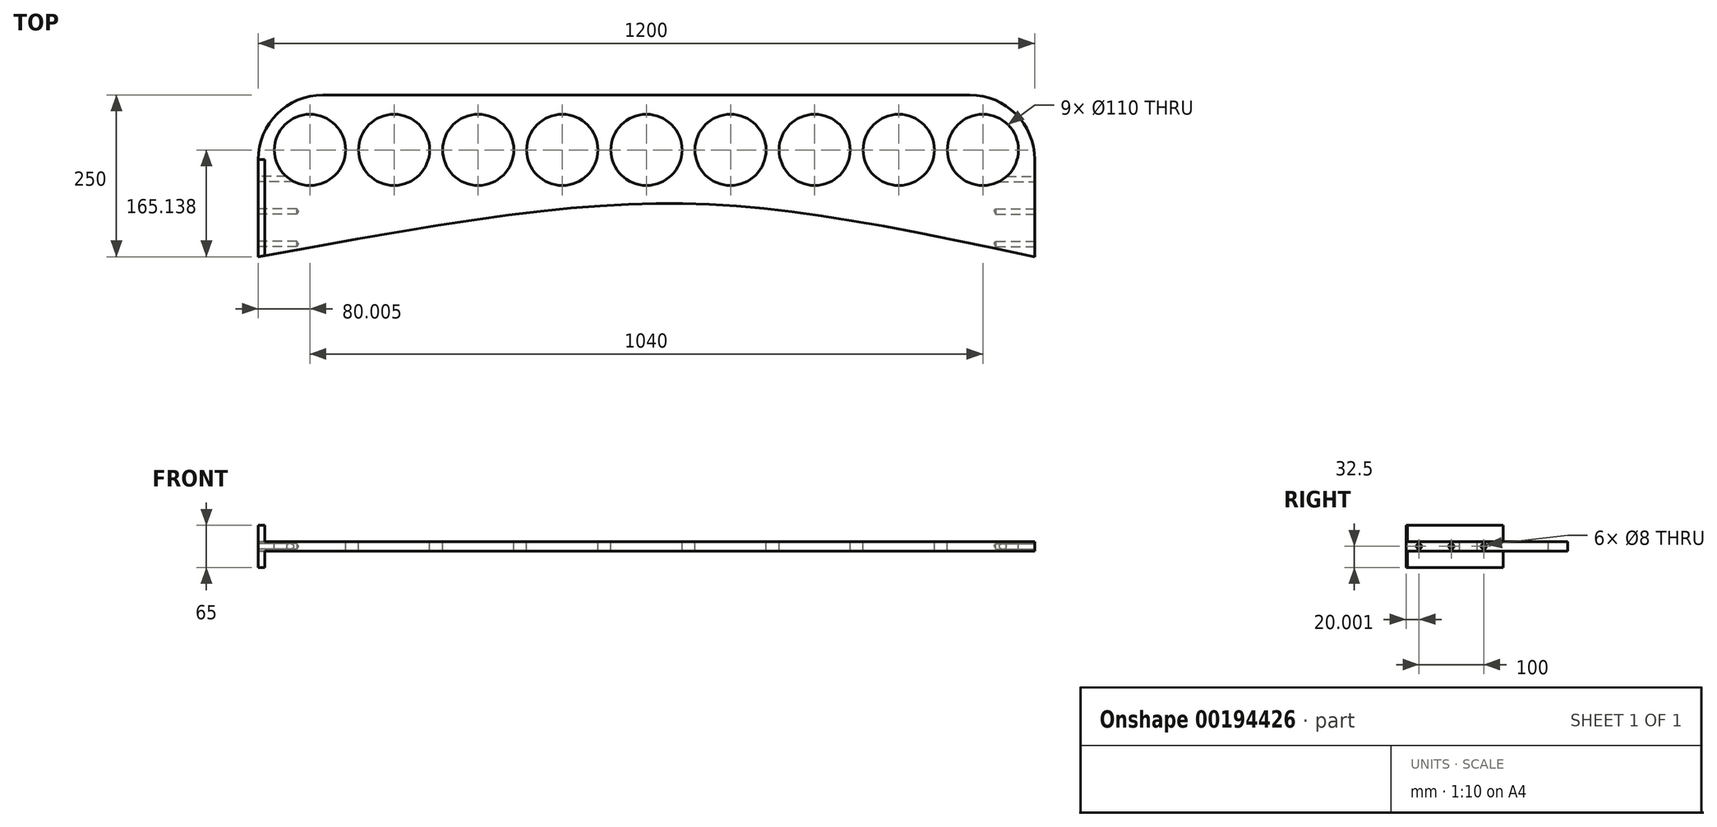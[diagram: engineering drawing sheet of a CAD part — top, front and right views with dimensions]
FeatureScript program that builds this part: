
annotation { "Feature Type Name" : "Feature", "Feature Type Description" : "" }
export const myFeature = defineFeature(function(context is Context, id is Id, definition is map)
    precondition{}
    {
        {
            var Q0;
            Q0=qCreatedBy(makeId("Top.planeOp"),FACE);
            var sketch = newSketch(context, id + "F0", { "sketchPlane" : qUnion([Q0])});
            skLineSegment(sketch, "E0", {"start": v(-982.08, 393.12) * mm, "end": v(217.92, 393.12) * mm});
            skLineSegment(sketch, "E1", {"start": v(217.92, 393.12) * mm, "end": v(217.92, 143.12) * mm});
            skLineSegment(sketch, "E2", {"start": v(217.92, 143.12) * mm, "end": v(-982.08, 143.12) * mm});
            skLineSegment(sketch, "E3", {"start": v(-982.08, 143.12) * mm, "end": v(-982.08, 393.12) * mm});
            skSolve(sketch);
        }
        {
            var Q0;
            Q0 = qSketchRegion(id + "F0", true);
            extrude(context, id + "F1", {"entities" : qUnion([Q0]), "depth" : 15 * mm});
        }
        {
            var Q0;
            Q0=makeQuery(id+"F1.opExtrude","CAP_FACE",FACE,{"disambiguationData":[OSD([sQuery(id+"F0.wireOp",EDGE,"E0"),sQuery(id+"F0.wireOp",EDGE,"E1"),sQuery(id+"F0.wireOp",EDGE,"E2"),sQuery(id+"F0.wireOp",EDGE,"E3")])],"isStart":false});
            var sketch = newSketch(context, id + "F2", { "sketchPlane" : qUnion([Q0])});
            skFitSpline(sketch, "E4", {"points": [v(-982.08, 143.12) * mm, v(217.92, 143.12) * mm], "startDerivative": vector(1802.84, 330) * mm, "endDerivative": vector(1542.06, -330) * mm});
            skSolve(sketch);
        }
        {
            var Q0;
            Q0=makeQuery(id+"F2.imprint","IMPRINT",FACE,{"disambiguationData":[TD([[makeQuery(id+"F2.imprint","IMPRINT",EDGE,{"derivedFrom":sQuery(id+"F2.wireOp",EDGE,"E4")}),-1.0]])]});
            extrude(context, id + "F3", {"entities" : qUnion([Q0]), "operationType" : NewBodyOperationType.REMOVE, "oppositeDirection" : true, "depth" : 25 * mm});
        }
        {
            var Q0;
            Q0=makeQuery(id+"F1.opExtrude","SWEPT_EDGE",EDGE,{"disambiguationData":[OSD([sQuery(id+"F0.wireOp",EDGE,"E0"),sQuery(id+"F0.wireOp",EDGE,"E3")])]});
            var Q1;
            Q1=makeQuery(id+"F1.opExtrude","SWEPT_EDGE",EDGE,{"disambiguationData":[OSD([sQuery(id+"F0.wireOp",EDGE,"E0"),sQuery(id+"F0.wireOp",EDGE,"E1")])]});
            fillet(context, id + "F4", {"entities" : qUnion([Q0, Q1]), "radius" : 100 * mm, "tangentPropagation" : true, "allowEdgeOverflow" : false});
        }
        {
            var Q0;
            Q0=makeQuery(id+"F1.opExtrude","SWEPT_FACE",FACE,{"disambiguationData":[OSD([sQuery(id+"F0.wireOp",EDGE,"E3")])]});
            var sketch = newSketch(context, id + "F5", { "sketchPlane" : qUnion([Q0])});
            skPoint(sketch, "E5", {"position": v(-163.12, 7.5) * mm});
            skPoint(sketch, "E5.positionSnap0", {"position": v(-143.12, 7.5) * mm});
            skPoint(sketch, "E6", {"position": v(-213.12, 7.5) * mm});
            skPoint(sketch, "E7", {"position": v(-263.12, 7.5) * mm});
            skSolve(sketch);
        }
        {
            var Q0;
            Q0=sQuery(id+"F5.wireOp",VERTEX,"E5");
            var Q1;
            Q1=sQuery(id+"F5.wireOp",VERTEX,"E6");
            var Q2;
            Q2=sQuery(id+"F5.wireOp",VERTEX,"E7");
            var Q3;
            Q3=makeQuery(id+"F1.opExtrude","SWEPT_BODY",BODY,{"disambiguationData":[OSD([sQuery(id+"F0.wireOp",EDGE,"E0"),sQuery(id+"F0.wireOp",EDGE,"E1"),sQuery(id+"F0.wireOp",EDGE,"E2"),sQuery(id+"F0.wireOp",EDGE,"E3")])]});
            hole(context, id + "F6", {"style" : HoleStyle.SIMPLE, "endStyle" : HoleEndStyle.BLIND, "holeDiameter" : 8 * mm, "holeDepth" : 60 * mm, "locations" : qUnion([Q0, Q1, Q2]), "scope" : qUnion([Q3])});
        }
        {
            var Q0;
            Q0=makeQuery(id+"F1.opExtrude","SWEPT_FACE",FACE,{"disambiguationData":[OSD([sQuery(id+"F0.wireOp",EDGE,"E1")])]});
            var sketch = newSketch(context, id + "F7", { "sketchPlane" : qUnion([Q0])});
            skPoint(sketch, "E8", {"position": v(163.12, 7.5) * mm});
            skPoint(sketch, "E8.positionSnap0", {"position": v(143.12, 7.5) * mm});
            skPoint(sketch, "E9", {"position": v(213.12, 7.5) * mm});
            skPoint(sketch, "E10", {"position": v(263.12, 7.5) * mm});
            skSolve(sketch);
        }
        {
            var Q0;
            Q0=sQuery(id+"F7.wireOp",VERTEX,"E8");
            var Q1;
            Q1=sQuery(id+"F7.wireOp",VERTEX,"E9");
            var Q2;
            Q2=sQuery(id+"F7.wireOp",VERTEX,"E10");
            var Q3;
            Q3=makeQuery(id+"F1.opExtrude","SWEPT_BODY",BODY,{"disambiguationData":[OSD([sQuery(id+"F0.wireOp",EDGE,"E0"),sQuery(id+"F0.wireOp",EDGE,"E1"),sQuery(id+"F0.wireOp",EDGE,"E2"),sQuery(id+"F0.wireOp",EDGE,"E3")])]});
            hole(context, id + "F8", {"style" : HoleStyle.SIMPLE, "endStyle" : HoleEndStyle.BLIND, "holeDiameter" : 8 * mm, "holeDepth" : 60 * mm, "locations" : qUnion([Q0, Q1, Q2]), "scope" : qUnion([Q3])});
        }
        {
            var Q0;
            Q0=makeQuery(id+"F1.opExtrude","CAP_FACE",FACE,{"disambiguationData":[OSD([sQuery(id+"F0.wireOp",EDGE,"E0"),sQuery(id+"F0.wireOp",EDGE,"E1"),sQuery(id+"F0.wireOp",EDGE,"E2"),sQuery(id+"F0.wireOp",EDGE,"E3")])],"isStart":false});
            var sketch = newSketch(context, id + "F9", { "sketchPlane" : qUnion([Q0])});
            skPoint(sketch, "E11", {"position": v(-382.08, 308.26) * mm});
            skPoint(sketch, "E11.positionSnap0", {"position": v(-382.08, 393.12) * mm});
            skCircle(sketch, "E12", {"center": v(-382.08, 308.26) * mm, "radius": 55 * mm});
            skPoint(sketch, "E13", {"position": v(-512.08, 308.26) * mm});
            skCircle(sketch, "E14", {"center": v(-512.08, 308.26) * mm, "radius": 55 * mm});
            skPoint(sketch, "E15", {"position": v(-642.08, 308.26) * mm});
            skPoint(sketch, "E16", {"position": v(-772.08, 308.26) * mm});
            skPoint(sketch, "E17", {"position": v(-902.08, 308.26) * mm});
            skCircle(sketch, "E18", {"center": v(-642.08, 308.26) * mm, "radius": 55 * mm});
            skCircle(sketch, "E19", {"center": v(-772.08, 308.26) * mm, "radius": 55 * mm});
            skCircle(sketch, "E20", {"center": v(-902.08, 308.26) * mm, "radius": 55 * mm});
            skPoint(sketch, "E21", {"position": v(-252.08, 308.26) * mm});
            skPoint(sketch, "E22", {"position": v(-122.08, 308.26) * mm});
            skPoint(sketch, "E23", {"position": v(7.92, 308.26) * mm});
            skPoint(sketch, "E24", {"position": v(137.92, 308.26) * mm});
            skCircle(sketch, "E25", {"center": v(-252.08, 308.26) * mm, "radius": 55 * mm});
            skCircle(sketch, "E26", {"center": v(-122.08, 308.26) * mm, "radius": 55 * mm});
            skCircle(sketch, "E27", {"center": v(7.92, 308.26) * mm, "radius": 55 * mm});
            skCircle(sketch, "E28", {"center": v(137.92, 308.26) * mm, "radius": 55 * mm});
            skSolve(sketch);
        }
        {
            var Q0;
            Q0=makeQuery(id+"F9.imprint","IMPRINT",FACE,{"disambiguationData":[TD([[makeQuery(id+"F9.imprint","IMPRINT",EDGE,{"derivedFrom":sQuery(id+"F9.wireOp",EDGE,"A5zAfX5e-1Hme-DiHA-6Irn-9hRMatuNrzMU")}),1.0]])]});
            var Q1;
            Q1=makeQuery(id+"F9.imprint","IMPRINT",FACE,{"disambiguationData":[TD([[makeQuery(id+"F9.imprint","IMPRINT",EDGE,{"derivedFrom":sQuery(id+"F9.wireOp",EDGE,"ykntFMBy-akwn-TRf7-CdXV-9nGkdkwRpkr6")}),1.0]])]});
            var Q2;
            Q2=makeQuery(id+"F9.imprint","IMPRINT",FACE,{"disambiguationData":[TD([[makeQuery(id+"F9.imprint","IMPRINT",EDGE,{"derivedFrom":sQuery(id+"F9.wireOp",EDGE,"gjbFzNf6-U6qb-g9FO-RQ4m-nnw1vyaDASKH")}),1.0]])]});
            var Q3;
            Q3=makeQuery(id+"F9.imprint","IMPRINT",FACE,{"disambiguationData":[TD([[makeQuery(id+"F9.imprint","IMPRINT",EDGE,{"derivedFrom":sQuery(id+"F9.wireOp",EDGE,"E20")}),1.0]])]});
            var Q4;
            Q4=makeQuery(id+"F9.imprint","IMPRINT",FACE,{"disambiguationData":[TD([[makeQuery(id+"F9.imprint","IMPRINT",EDGE,{"derivedFrom":sQuery(id+"F9.wireOp",EDGE,"E19")}),1.0]])]});
            var Q5;
            Q5=makeQuery(id+"F9.imprint","IMPRINT",FACE,{"disambiguationData":[TD([[makeQuery(id+"F9.imprint","IMPRINT",EDGE,{"derivedFrom":sQuery(id+"F9.wireOp",EDGE,"E18")}),1.0]])]});
            var Q6;
            Q6=makeQuery(id+"F9.imprint","IMPRINT",FACE,{"disambiguationData":[TD([[makeQuery(id+"F9.imprint","IMPRINT",EDGE,{"derivedFrom":sQuery(id+"F9.wireOp",EDGE,"E14")}),1.0]])]});
            var Q7;
            Q7=makeQuery(id+"F9.imprint","IMPRINT",FACE,{"disambiguationData":[TD([[makeQuery(id+"F9.imprint","IMPRINT",EDGE,{"derivedFrom":sQuery(id+"F9.wireOp",EDGE,"E12")}),1.0]])]});
            var Q8;
            Q8=makeQuery(id+"F9.imprint","IMPRINT",FACE,{"disambiguationData":[TD([[makeQuery(id+"F9.imprint","IMPRINT",EDGE,{"derivedFrom":sQuery(id+"F9.wireOp",EDGE,"E25")}),1.0]])]});
            var Q9;
            Q9=makeQuery(id+"F9.imprint","IMPRINT",FACE,{"disambiguationData":[TD([[makeQuery(id+"F9.imprint","IMPRINT",EDGE,{"derivedFrom":sQuery(id+"F9.wireOp",EDGE,"E26")}),1.0]])]});
            var Q10;
            Q10=makeQuery(id+"F9.imprint","IMPRINT",FACE,{"disambiguationData":[TD([[makeQuery(id+"F9.imprint","IMPRINT",EDGE,{"derivedFrom":sQuery(id+"F9.wireOp",EDGE,"E27")}),1.0]])]});
            var Q11;
            Q11=makeQuery(id+"F9.imprint","IMPRINT",FACE,{"disambiguationData":[TD([[makeQuery(id+"F9.imprint","IMPRINT",EDGE,{"derivedFrom":sQuery(id+"F9.wireOp",EDGE,"E28")}),1.0]])]});
            extrude(context, id + "F10", {"entities" : qUnion([Q0, Q1, Q2, Q3, Q4, Q5, Q6, Q7, Q8, Q9, Q10, Q11]), "operationType" : NewBodyOperationType.REMOVE, "oppositeDirection" : true, "depth" : 25 * mm});
        }
        {
            var Q0;
            Q0=makeQuery(id+"F1.opExtrude","CAP_FACE",FACE,{"disambiguationData":[OSD([sQuery(id+"F0.wireOp",EDGE,"E0"),sQuery(id+"F0.wireOp",EDGE,"E1"),sQuery(id+"F0.wireOp",EDGE,"E2"),sQuery(id+"F0.wireOp",EDGE,"E3")])],"isStart":true});
            var sketch = newSketch(context, id + "F11", { "sketchPlane" : qUnion([Q0])});
            skLineSegment(sketch, "E29.bottom", {"start": v(-982.08, -143.12) * mm, "end": v(-972.08, -143.12) * mm});
            skLineSegment(sketch, "E29.top", {"start": v(-982.08, -293.12) * mm, "end": v(-972.08, -293.12) * mm});
            skLineSegment(sketch, "E29.left", {"start": v(-982.08, -143.12) * mm, "end": v(-982.08, -293.12) * mm});
            skLineSegment(sketch, "E29.right", {"start": v(-972.08, -143.12) * mm, "end": v(-972.08, -293.12) * mm});
            skSolve(sketch);
        }
        {
            var Q0;
            {var subQ0=sQuery(id+"F11.wireOp",EDGE,"E29.top");Q0=makeQuery(id+"F11.imprint","IMPRINT",FACE,{"disambiguationData":[TD([[makeQuery(id+"F11.imprint","IMPRINT",EDGE,{"derivedFrom":subQ0}),1.0]])]});}
            extrude(context, id + "F12", {"entities" : qUnion([Q0]), "operationType" : NewBodyOperationType.ADD, "depth" : 25 * mm, "offsetDistance" : 25 * mm});
        }
        {
            var Q0;
            Q0=makeQuery(id+"F1.opExtrude","CAP_FACE",FACE,{"disambiguationData":[OSD([sQuery(id+"F0.wireOp",EDGE,"E0"),sQuery(id+"F0.wireOp",EDGE,"E1"),sQuery(id+"F0.wireOp",EDGE,"E2"),sQuery(id+"F0.wireOp",EDGE,"E3")])],"isStart":false});
            var sketch = newSketch(context, id + "F13", { "sketchPlane" : qUnion([Q0])});
            skLineSegment(sketch, "E30.bottom", {"start": v(-982.08, 143.12) * mm, "end": v(-972.08, 143.12) * mm});
            skLineSegment(sketch, "E30.top", {"start": v(-982.08, 293.12) * mm, "end": v(-972.08, 293.12) * mm});
            skLineSegment(sketch, "E30.left", {"start": v(-982.08, 143.12) * mm, "end": v(-982.08, 293.12) * mm});
            skLineSegment(sketch, "E30.right", {"start": v(-972.08, 143.12) * mm, "end": v(-972.08, 293.12) * mm});
            skSolve(sketch);
        }
        {
            var Q0;
            {var subQ0=sQuery(id+"F13.wireOp",EDGE,"E30.top");Q0=makeQuery(id+"F13.imprint","IMPRINT",FACE,{"disambiguationData":[TD([[makeQuery(id+"F13.imprint","IMPRINT",EDGE,{"derivedFrom":subQ0}),-1.0]])]});}
            extrude(context, id + "F14", {"entities" : qUnion([Q0]), "operationType" : NewBodyOperationType.ADD, "depth" : 25 * mm, "offsetDistance" : 25 * mm});
        }
    });
